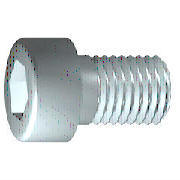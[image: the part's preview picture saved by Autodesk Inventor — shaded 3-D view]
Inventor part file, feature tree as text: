
AUTODESK INVENTOR PART (.ipt)
format: ipt  version: 2016 (Build 200138000, 138)  size: 190,464 bytes
history: native  units: mm (DEFAULTED — no unit token found)
features: sketch x2, other x1, extrude x1, plane x1, fillet x1
ambient origin geometry x7: Origin, YZ Plane, XY Plane, X Axis, Y Axis, Z Axis, Center Point
bodies: Solid1 (feature_tree)
feature tree (6):
  other  "Körper"
  extrude  "Loch"  Depth=3.0mm
  plane  "Work Plane1"
  fillet  "Fillet2"  Radius=3.0mm
  sketch  "Skizze1"  dims[d1=10.75mm d2=0.306825mm d3=3.0mm]
  sketch  "Skizze2"  dims[d4=1.3mm d5=60.0deg d6=3.0mm d7=3.0mm d8=2.886751mm d9=5.5mm d10=90.0deg d11=10.0mm d12=0.0mm d13=10.75mm d14=0.0mm d15=0.306725mm d16=0.306725mm d17=0.3mm d19=0.0mm d26=12.0mm d27=45.0deg d28=0.0mm d29=0.0mm d30=0.1mm]
